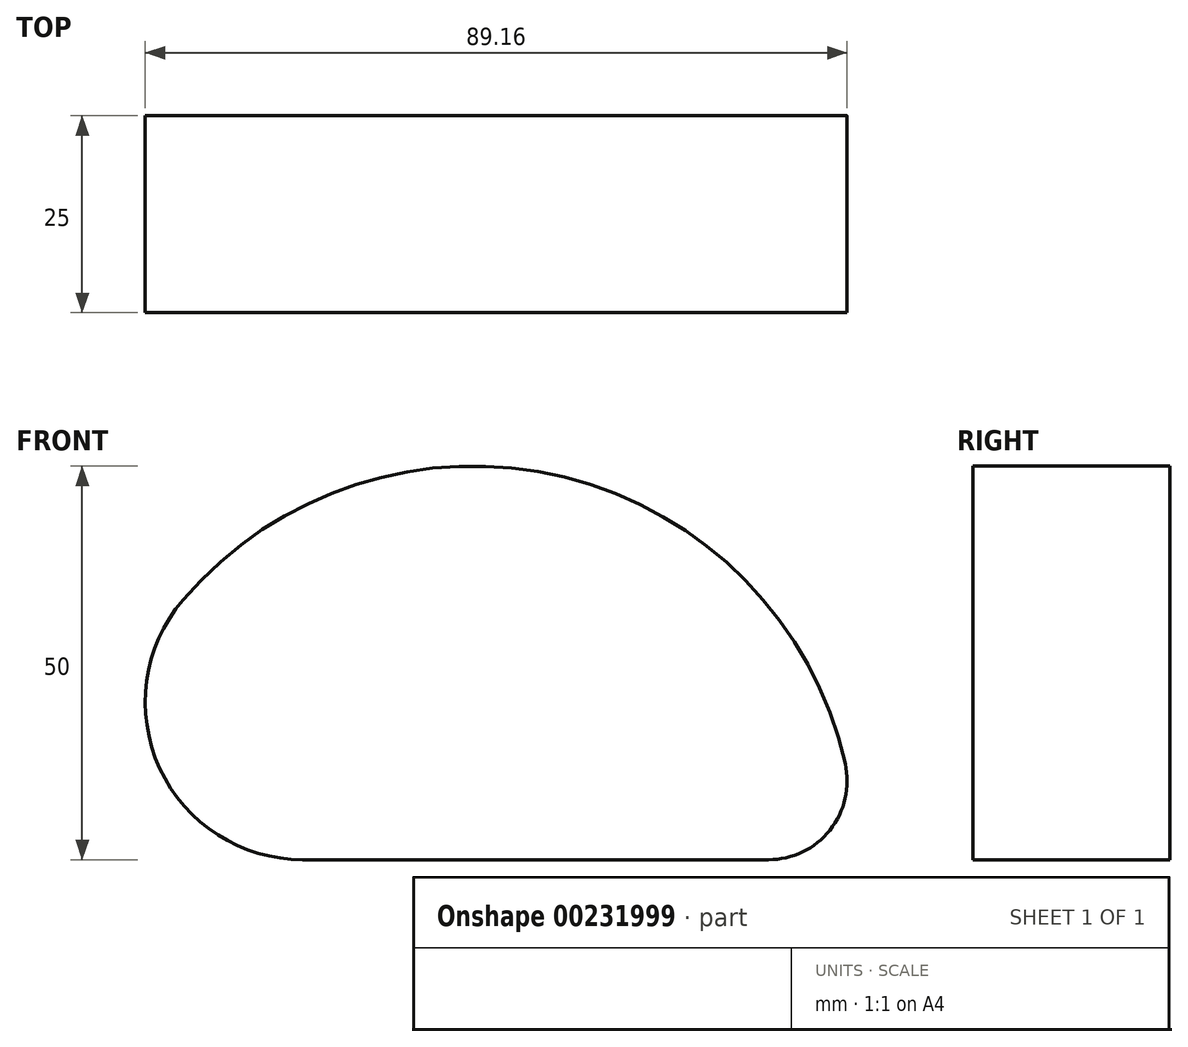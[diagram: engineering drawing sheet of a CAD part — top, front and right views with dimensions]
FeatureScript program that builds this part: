
annotation { "Feature Type Name" : "Feature", "Feature Type Description" : "" }
export const myFeature = defineFeature(function(context is Context, id is Id, definition is map)
    precondition{}
    {
        {
            var Q0;
            Q0=qCreatedBy(makeId("Front.planeOp"),FACE);
            var sketch = newSketch(context, id + "F0", { "sketchPlane" : qUnion([Q0])});
            skLineSegment(sketch, "E0", {"start": v(-32.03, -16.05) * mm, "end": v(27.13, -16.05) * mm});
            skArc(sketch, "E1", {"start": v(-32.03, -16.05) * mm, "mid": v(-50.18, -4.43) * mm, "end": v(-47.25, 16.92) * mm});
            skArc(sketch, "E2", {"start": v(27.13, -16.05) * mm, "mid": v(34.94, -12.3) * mm, "end": v(36.89, -3.85) * mm});
            skArc(sketch, "E3", {"start": v(-47.25, 16.92) * mm, "mid": v(1.24, 32.54) * mm, "end": v(36.89, -3.85) * mm});
            skSolve(sketch);
        }
        {
            var Q0;
            Q0=makeQuery(id+"F0.imprint","IMPRINT",FACE,{"disambiguationData":[TD([[makeQuery(id+"F0.imprint","IMPRINT",EDGE,{"derivedFrom":sQuery(id+"F0.wireOp",EDGE,"E0")}),1.0]])]});
            extrude(context, id + "F1", {"entities" : qUnion([Q0]), "depth" : 25 * mm});
        }
    });
